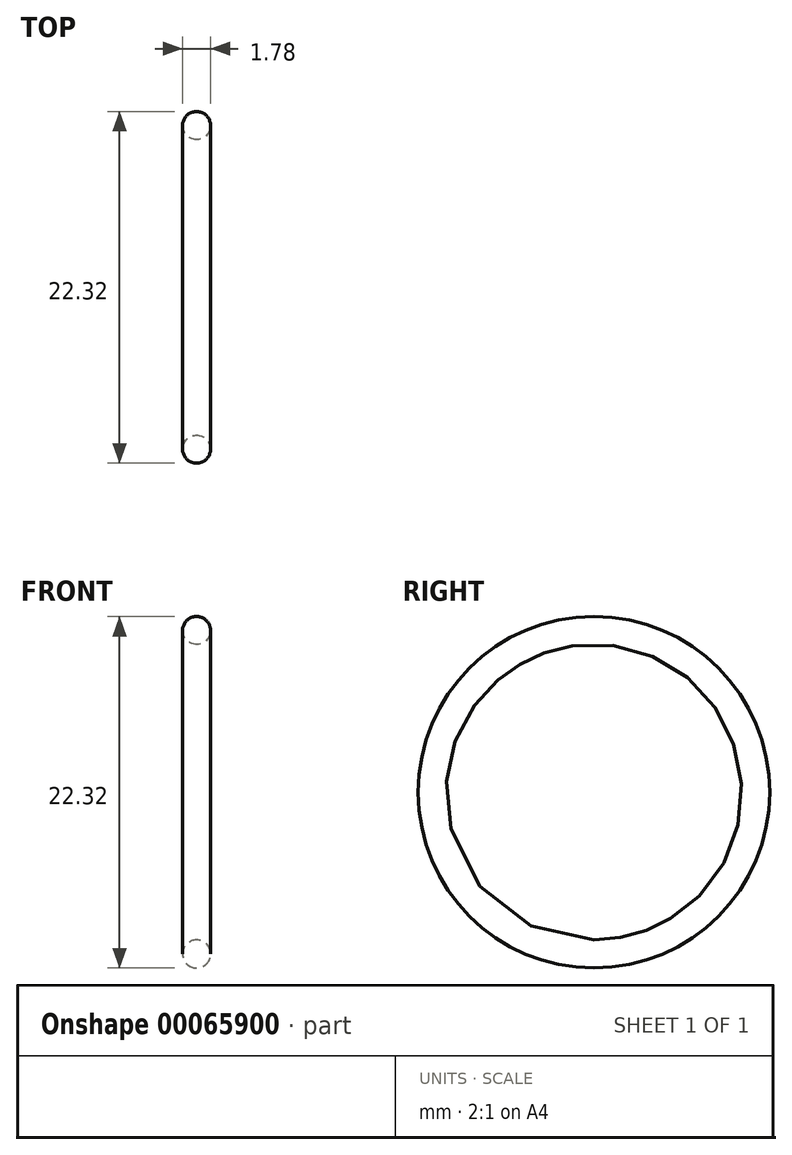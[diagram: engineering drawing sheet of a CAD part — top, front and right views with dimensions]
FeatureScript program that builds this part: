
annotation { "Feature Type Name" : "Feature", "Feature Type Description" : "" }
export const myFeature = defineFeature(function(context is Context, id is Id, definition is map)
    precondition{}
    {
        {
            var Q0;
            Q0=qCreatedBy(makeId("Front.planeOp"),FACE);
            var sketch = newSketch(context, id + "F0", { "sketchPlane" : qUnion([Q0])});
            skLineSegment(sketch, "E0", {"start": v(0, 0) * mm, "end": v(-6.06, 0) * mm, "construction": true});
            skCircle(sketch, "E1", {"center": v(0, 10.27) * mm, "radius": 0.89 * mm});
            skSolve(sketch);
        }
        {
            var Q0;
            Q0=makeQuery(id+"F0.imprint","IMPRINT",FACE,{"disambiguationData":[TD([[makeQuery(id+"F0.imprint","IMPRINT",EDGE,{"derivedFrom":sQuery(id+"F0.wireOp",EDGE,"E1")}),1.0]])]});
            var Q1;
            Q1=sQuery(id+"F0.wireOp",EDGE,"E0");
            revolve(context, id + "F1", {"entities" : qUnion([Q0]), "axis" : qUnion([Q1]), "revolveType" : RevolveType.FULL});
        }
    });
